# Revit family: VT.TECHNOMIX.0
name_source: partatom
category: Оборудование
units: mm (PartAtom-declared; Revit-internal decimal feet)

## family parameters
Всегда вертикально = Да
Заголовок OmniClass = Climate Control (HVAC)
На основе рабочей плоскости = Нет
Номер OmniClass = 23.75.00.00
Общий = Нет
При загрузке вырезать с полостями = Нет
Размер круглого соединителя = Использовать диаметр
Тип детали = Нормальный
Точка расчета площади = Нет

## types (1)
- VT.TECHNOMIX.0
    BIMобъект основная категория = Водопровод
    EMCS Version = 3.0
    Family Version = Rev.00
    IFC классификация = Клапан
    Max рабочая температура = 100 °C
    Max рабочее давление = 1000000.0 Па
    Revit Version = 2018
    URL = https://valtec.ru
    URL бренда = https://valtec.ru
    URL продукта = https://valtec.ru
    Uniclass 1.4 Описание = Клапаны
    Uniclass 2.0 Описание = Клапаны
    Uniclass 2015 Name = Системы отопления, охлаждения и охлаждения
    Uniformat II Описание = HVAC
    Weight Net (Kg) = 0
    Гидравлический возвратный поток = 0.0 л/с
    Гидравлический поток подачи = 0.0 л/с
    Группа модели = Смесительные узлы и клапаны
    Группа товаров = Насосно-смесительный узел VALTEC TECHNOMIX
    Изготовитель = IVAR
    Инструкции по установке = https://valtec.ru
    Код категории BIMобъекта = Водопроводным-дополнительный
    Код основной категории BIMobject = Водопровод
    Линия продуктов = Смесительные узлы и клапаны
    Мастерформат 2014 Описание = Отопление, вентиляция и кондиционирование воздуха (HVAC)
    Материал = Nickel-plated brass - CW617N
    Материал вторичный = Copper
    Материал основной = Brass
    Название производителя = IVAR
    Насосное пространство = 130 мм
    Номинальная высота = 0 мм
    Номинальная ширина = 0 мм
    Общий поток подачи гидравлики = 0.0 л/с
    Описание = TECHNOMIX блок регулятора для систем отопления
    Описание NBS = Клапаны
    Описание OmniClass = Клапаны
    Описание Конфигурации = Блок регулятора TECHNOMIX для излучающих систем.
    Описание статьи = TECHNOMIX блок регулятора для систем отопления
    Полный гидравлический возвратный поток = 0.0 л/с
    Продукт SKU = TECHNOMIX
    Произведено в = Сделано в Италии
    Размер соединения = G 1"
    Размеры соединения насоса = G 1"1/2F flat seal
    Страна производитель = Italy
    Техническое описание = https://valtec.ru
    Тип статьи = Смесительные узлы и клапаны
